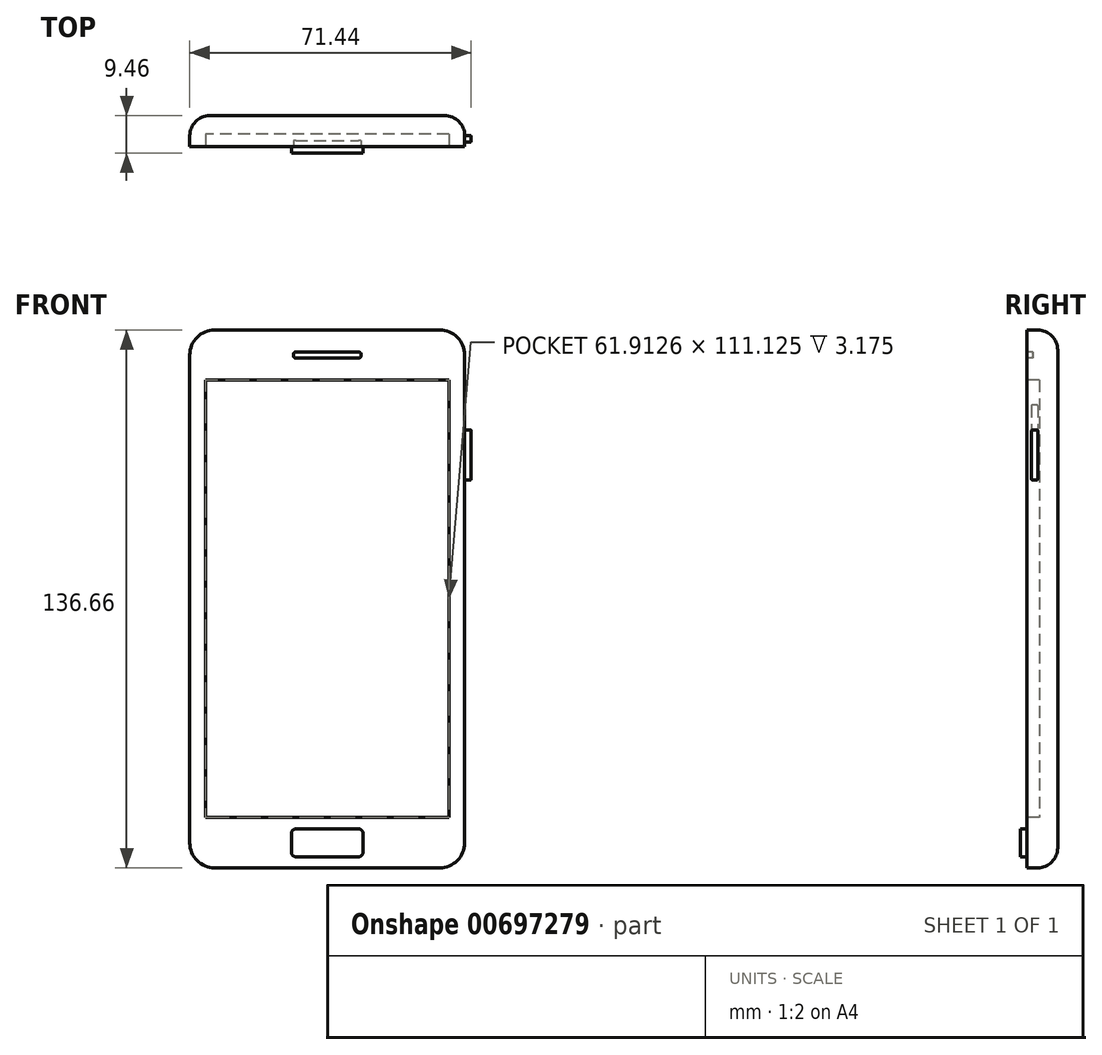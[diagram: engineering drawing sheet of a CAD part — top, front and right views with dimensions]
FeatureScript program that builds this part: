
annotation { "Feature Type Name" : "Feature", "Feature Type Description" : "" }
export const myFeature = defineFeature(function(context is Context, id is Id, definition is map)
    precondition{}
    {
        {
            var Q0;
            Q0=qCreatedBy(makeId("Front.planeOp"),FACE);
            var sketch = newSketch(context, id + "F0", { "sketchPlane" : qUnion([Q0])});
            skLineSegment(sketch, "E0", {"start": v(-34.93, 61.98) * mm, "end": v(-34.93, -61.98) * mm});
            skLineSegment(sketch, "E1", {"start": v(-28.58, 68.33) * mm, "end": v(28.57, 68.33) * mm});
            skLineSegment(sketch, "E2", {"start": v(34.92, 61.98) * mm, "end": v(34.92, -61.98) * mm});
            skLineSegment(sketch, "E3", {"start": v(28.57, -68.33) * mm, "end": v(-28.58, -68.33) * mm});
            skPoint(sketch, "E4.visualSharp", {"position": v(-34.93, 68.33) * mm});
            skArc(sketch, "E4.filletArc", {"start": v(-28.58, 68.33) * mm, "mid": v(-33.07, 66.47) * mm, "end": v(-34.93, 61.98) * mm});
            skPoint(sketch, "E5.visualSharp", {"position": v(34.92, 68.33) * mm});
            skArc(sketch, "E5.filletArc", {"start": v(34.92, 61.98) * mm, "mid": v(33.07, 66.47) * mm, "end": v(28.57, 68.33) * mm});
            skLineSegment(sketch, "E6", {"start": v(0, 68.33) * mm, "end": v(0, -68.33) * mm, "construction": true});
            skPoint(sketch, "E7.visualSharp", {"position": v(-34.93, -68.33) * mm});
            skArc(sketch, "E7.filletArc", {"start": v(-34.93, -61.98) * mm, "mid": v(-33.07, -66.47) * mm, "end": v(-28.58, -68.33) * mm});
            skPoint(sketch, "E8.visualSharp", {"position": v(34.92, -68.33) * mm});
            skArc(sketch, "E8.filletArc", {"start": v(28.57, -68.33) * mm, "mid": v(33.07, -66.47) * mm, "end": v(34.92, -61.98) * mm});
            skLineSegment(sketch, "E9", {"start": v(-34.93, 0) * mm, "end": v(34.92, 0) * mm, "construction": true});
            skLineSegment(sketch, "E10", {"start": v(-34.93, -61.98) * mm, "end": v(34.92, -61.98) * mm, "construction": true});
            skLineSegment(sketch, "E11", {"start": v(-34.93, 61.98) * mm, "end": v(34.92, 61.98) * mm, "construction": true});
            skSolve(sketch);
        }
        {
            var Q0;
            Q0=makeQuery(id+"F0.imprint","IMPRINT",FACE,{"disambiguationData":[TD([[makeQuery(id+"F0.imprint","IMPRINT",EDGE,{"derivedFrom":sQuery(id+"F0.wireOp",EDGE,"E0")}),1.0]])]});
            var Q1;
            Q1=makeQuery(id+"F0.imprint","IMPRINT",FACE,{"disambiguationData":[TD([[makeQuery(id+"F0.imprint","IMPRINT",EDGE,{"derivedFrom":sQuery(id+"F0.wireOp",EDGE,"Yxqkso8f-ke1d-uWKi-IK2T-4UMQfv2AGNoA")}),-1.0]])]});
            var Q2;
            Q2=makeQuery(id+"F0.imprint","IMPRINT",FACE,{"disambiguationData":[TD([[makeQuery(id+"F0.imprint","IMPRINT",EDGE,{"derivedFrom":sQuery(id+"F0.wireOp",EDGE,"Q10cRNlM-3Szw-gUv3-p6k7-crAdpTybPVzU")}),-1.0]])]});
            extrude(context, id + "F1", {"entities" : qUnion([Q0, Q1, Q2]), "depth" : 7.87 * mm, "offsetDistance" : 25.4 * mm});
        }
        {
            var Q0;
            Q0=makeQuery(id+"F1.opExtrude","CAP_EDGE",EDGE,{"disambiguationData":[OSD([sQuery(id+"F0.wireOp",EDGE,"E5.filletArc")])],"isStart":true});
            var Q1;
            Q1=makeQuery(id+"F1.opExtrude","CAP_EDGE",EDGE,{"disambiguationData":[OSD([sQuery(id+"F0.wireOp",EDGE,"E1")])],"isStart":true});
            var Q2;
            Q2=makeQuery(id+"F1.opExtrude","CAP_EDGE",EDGE,{"disambiguationData":[OSD([sQuery(id+"F0.wireOp",EDGE,"E2")])],"isStart":true});
            fillet(context, id + "F2", {"entities" : qUnion([Q0, Q1, Q2]), "radius" : 5.08 * mm, "tangentPropagation" : true, "allowEdgeOverflow" : false});
        }
        {
            var Q0;
            Q0=makeQuery(id+"F1.opExtrude","CAP_FACE",FACE,{"disambiguationData":[OSD([sQuery(id+"F0.wireOp",EDGE,"E0"),sQuery(id+"F0.wireOp",EDGE,"E1"),sQuery(id+"F0.wireOp",EDGE,"E2"),sQuery(id+"F0.wireOp",EDGE,"E3"),sQuery(id+"F0.wireOp",EDGE,"E4.filletArc"),sQuery(id+"F0.wireOp",EDGE,"E5.filletArc"),sQuery(id+"F0.wireOp",EDGE,"E7.filletArc"),sQuery(id+"F0.wireOp",EDGE,"E8.filletArc"),sQuery(id+"F0.wireOp",EDGE,"Yxqkso8f-ke1d-uWKi-IK2T-4UMQfv2AGNoA"),sQuery(id+"F0.wireOp",EDGE,"wvmofA8N-cZgQ-HB6A-NeT5-mTsQP75NdnSN"),sQuery(id+"F0.wireOp",EDGE,"2k0ZVNAU-dHE0-9XoG-fVzd-rWTm6Z1FSZgh"),sQuery(id+"F0.wireOp",EDGE,"L0vu10QN-11z5-3LHw-4cct-LfvSpySfau56"),sQuery(id+"F0.wireOp",EDGE,"61cbf7f2-a8a0-450c-8582-404ff57eee1e.filletArc"),sQuery(id+"F0.wireOp",EDGE,"9b09c1d2-0208-4afe-876b-a53897a61bd5.filletArc"),sQuery(id+"F0.wireOp",EDGE,"2e49db2c-9e25-4e03-abbd-2e55815f41f9.filletArc"),sQuery(id+"F0.wireOp",EDGE,"847fe96b-3720-45e1-b239-618744106075.filletArc"),sQuery(id+"F0.wireOp",EDGE,"Q10cRNlM-3Szw-gUv3-p6k7-crAdpTybPVzU"),sQuery(id+"F0.wireOp",EDGE,"rr5Ry5rM-HqL5-93G9-RZ6w-pYJKNWClKjOs"),sQuery(id+"F0.wireOp",EDGE,"Tm6RvqHi-hzwC-IS7W-cwuA-Y99RD3NHICGs"),sQuery(id+"F0.wireOp",EDGE,"gLD1SR3Y-jlRX-iXej-22FT-tG82X233p80r"),sQuery(id+"F0.wireOp",EDGE,"53dd5e3a-b83d-4c4f-a617-f595e198c785.filletArc"),sQuery(id+"F0.wireOp",EDGE,"2cd74231-fede-4f60-8454-4e1e7671c0d9.filletArc"),sQuery(id+"F0.wireOp",EDGE,"ae25c646-67f5-4699-874b-49e99440fea7.filletArc"),sQuery(id+"F0.wireOp",EDGE,"5c01ee20-0546-43ea-a8ab-d59d5ab6d27c.filletArc")])],"isStart":false});
            var sketch = newSketch(context, id + "F3", { "sketchPlane" : qUnion([Q0])});
            skLineSegment(sketch, "E12", {"start": v(-30.96, 55.56) * mm, "end": v(-30.96, -55.56) * mm});
            skLineSegment(sketch, "E13", {"start": v(-30.96, -55.56) * mm, "end": v(30.96, -55.56) * mm});
            skLineSegment(sketch, "E14", {"start": v(30.96, -55.56) * mm, "end": v(30.96, 55.56) * mm});
            skLineSegment(sketch, "E15", {"start": v(30.96, 55.56) * mm, "end": v(-30.96, 55.56) * mm});
            skLineSegment(sketch, "E16", {"start": v(0, 55.56) * mm, "end": v(0, -55.56) * mm, "construction": true});
            skLineSegment(sketch, "E17", {"start": v(30.96, 0) * mm, "end": v(-30.96, 0) * mm, "construction": true});
            skPoint(sketch, "E17.endSnap0", {"position": v(-34.93, 0) * mm});
            skLineSegment(sketch, "E18", {"start": v(-7.94, 62.77) * mm, "end": v(7.94, 62.77) * mm});
            skLineSegment(sketch, "E19", {"start": v(8.61, 62.1) * mm, "end": v(8.61, 61.86) * mm});
            skLineSegment(sketch, "E20", {"start": v(7.94, 61.18) * mm, "end": v(-7.94, 61.18) * mm});
            skLineSegment(sketch, "E21", {"start": v(-8.61, 61.86) * mm, "end": v(-8.61, 62.1) * mm});
            skArc(sketch, "E22.filletArc", {"start": v(8.61, 62.1) * mm, "mid": v(8.41, 62.57) * mm, "end": v(7.94, 62.77) * mm});
            skArc(sketch, "E23.filletArc", {"start": v(7.94, 61.18) * mm, "mid": v(8.41, 61.38) * mm, "end": v(8.61, 61.86) * mm});
            skArc(sketch, "E24.filletArc", {"start": v(-7.94, 62.77) * mm, "mid": v(-8.41, 62.57) * mm, "end": v(-8.61, 62.1) * mm});
            skArc(sketch, "E25.filletArc", {"start": v(-8.61, 61.86) * mm, "mid": v(-8.41, 61.38) * mm, "end": v(-7.94, 61.18) * mm});
            skLineSegment(sketch, "E26", {"start": v(0, 62.77) * mm, "end": v(0, 61.18) * mm, "construction": true});
            skLineSegment(sketch, "E27", {"start": v(8.61, 61.98) * mm, "end": v(-8.61, 61.98) * mm, "construction": true});
            skSolve(sketch);
        }
        {
            var Q0;
            Q0=makeQuery(id+"F3.imprint","IMPRINT",FACE,{"disambiguationData":[TD([[makeQuery(id+"F3.imprint","IMPRINT",EDGE,{"derivedFrom":sQuery(id+"F3.wireOp",EDGE,"E12")}),1.0]])]});
            extrude(context, id + "F4", {"entities" : qUnion([Q0]), "operationType" : NewBodyOperationType.REMOVE, "oppositeDirection" : true, "depth" : 3.17 * mm, "offsetDistance" : 25.4 * mm});
        }
        {
            var Q0;
            Q0=makeQuery(id+"F3.imprint","IMPRINT",FACE,{"disambiguationData":[TD([[makeQuery(id+"F3.imprint","IMPRINT",EDGE,{"derivedFrom":sQuery(id+"F3.wireOp",EDGE,"E12")}),-1.0]])]});
            var sketch = newSketch(context, id + "F5", { "sketchPlane" : qUnion([Q0])});
            skLineSegment(sketch, "E28", {"start": v(-7.94, -58.43) * mm, "end": v(7.94, -58.43) * mm});
            skLineSegment(sketch, "E29", {"start": v(-9.1, -59.6) * mm, "end": v(-9.1, -64.36) * mm});
            skLineSegment(sketch, "E30", {"start": v(9.1, -59.6) * mm, "end": v(9.1, -64.36) * mm});
            skLineSegment(sketch, "E31", {"start": v(7.94, -65.52) * mm, "end": v(-7.94, -65.52) * mm});
            skArc(sketch, "E32.filletArc", {"start": v(-7.94, -58.43) * mm, "mid": v(-8.76, -58.77) * mm, "end": v(-9.1, -59.6) * mm});
            skArc(sketch, "E33.filletArc", {"start": v(-9.1, -64.36) * mm, "mid": v(-8.76, -65.18) * mm, "end": v(-7.94, -65.52) * mm});
            skArc(sketch, "E34.filletArc", {"start": v(9.1, -59.6) * mm, "mid": v(8.76, -58.77) * mm, "end": v(7.94, -58.43) * mm});
            skArc(sketch, "E35.filletArc", {"start": v(7.94, -65.52) * mm, "mid": v(8.76, -65.18) * mm, "end": v(9.1, -64.36) * mm});
            skLineSegment(sketch, "E36", {"start": v(0, -58.43) * mm, "end": v(0, -65.52) * mm, "construction": true});
            skLineSegment(sketch, "E37", {"start": v(-9.1, -61.98) * mm, "end": v(9.1, -61.98) * mm, "construction": true});
            skSolve(sketch);
        }
        {
            var Q0;
            Q0=makeQuery(id+"F5.imprint","IMPRINT",FACE,{"disambiguationData":[TD([[makeQuery(id+"F5.imprint","IMPRINT",EDGE,{"derivedFrom":sQuery(id+"F5.wireOp",EDGE,"E28")}),-1.0]])]});
            extrude(context, id + "F6", {"entities" : qUnion([Q0]), "operationType" : NewBodyOperationType.ADD, "depth" : 1.59 * mm, "offsetDistance" : 25.4 * mm});
        }
        {
            var Q0;
            Q0=makeQuery(id+"F3.imprint","IMPRINT",FACE,{"disambiguationData":[TD([[makeQuery(id+"F3.imprint","IMPRINT",EDGE,{"derivedFrom":sQuery(id+"F3.wireOp",EDGE,"E18")}),-1.0]])]});
            extrude(context, id + "F7", {"entities" : qUnion([Q0]), "operationType" : NewBodyOperationType.REMOVE, "oppositeDirection" : true, "depth" : 1.59 * mm, "offsetDistance" : 25.4 * mm});
        }
        {
            var Q0;
            Q0=makeQuery(id+"F1.opExtrude","SWEPT_FACE",FACE,{"disambiguationData":[OSD([sQuery(id+"F0.wireOp",EDGE,"E0")])]});
            var sketch = newSketch(context, id + "F8", { "sketchPlane" : qUnion([Q0])});
            skLineSegment(sketch, "E38", {"start": v(6.67, 49.05) * mm, "end": v(6.67, 30.45) * mm});
            skLineSegment(sketch, "E39", {"start": v(6.44, 30.23) * mm, "end": v(5.3, 30.23) * mm});
            skLineSegment(sketch, "E40", {"start": v(5.08, 30.45) * mm, "end": v(5.08, 49.05) * mm});
            skLineSegment(sketch, "E41", {"start": v(5.3, 49.28) * mm, "end": v(6.44, 49.28) * mm});
            skLineSegment(sketch, "E42", {"start": v(6.67, 39.75) * mm, "end": v(5.08, 39.75) * mm, "construction": true});
            skPoint(sketch, "E43.visualSharp", {"position": v(6.67, 49.28) * mm});
            skArc(sketch, "E43.filletArc", {"start": v(6.67, 49.05) * mm, "mid": v(6.6, 49.2) * mm, "end": v(6.44, 49.28) * mm});
            skPoint(sketch, "E44.visualSharp", {"position": v(5.08, 49.28) * mm});
            skArc(sketch, "E44.filletArc", {"start": v(5.3, 49.28) * mm, "mid": v(5.15, 49.2) * mm, "end": v(5.08, 49.05) * mm});
            skPoint(sketch, "E45.visualSharp", {"position": v(6.67, 30.23) * mm});
            skArc(sketch, "E45.filletArc", {"start": v(6.44, 30.23) * mm, "mid": v(6.6, 30.3) * mm, "end": v(6.67, 30.45) * mm});
            skPoint(sketch, "E46.visualSharp", {"position": v(5.08, 30.23) * mm});
            skArc(sketch, "E46.filletArc", {"start": v(5.08, 30.45) * mm, "mid": v(5.15, 30.3) * mm, "end": v(5.3, 30.23) * mm});
            skSolve(sketch);
        }
        {
            var Q0;
            Q0=makeQuery(id+"F8.imprint","IMPRINT",FACE,{"disambiguationData":[TD([[makeQuery(id+"F8.imprint","IMPRINT",EDGE,{"derivedFrom":sQuery(id+"F8.wireOp",EDGE,"E41")}),-1.0]])]});
            var Q1;
            Q1=makeQuery(id+"F8.imprint","IMPRINT",FACE,{"disambiguationData":[TD([[makeQuery(id+"F8.imprint","IMPRINT",EDGE,{"derivedFrom":sQuery(id+"F8.wireOp",EDGE,"E39")}),-1.0]])]});
            extrude(context, id + "F9", {"entities" : qUnion([Q0, Q1]), "operationType" : NewBodyOperationType.ADD, "depth" : 1 / 406.4 * mm, "offsetDistance" : 25.4 * mm});
        }
        {
            var Q0;
            Q0=makeQuery(id+"F1.opExtrude","SWEPT_FACE",FACE,{"disambiguationData":[OSD([sQuery(id+"F0.wireOp",EDGE,"E2")])]});
            var sketch = newSketch(context, id + "F10", { "sketchPlane" : qUnion([Q0])});
            skLineSegment(sketch, "E47", {"start": v(-5.08, 42.7) * mm, "end": v(-5.08, 30.45) * mm});
            skLineSegment(sketch, "E48", {"start": v(-5.3, 30.23) * mm, "end": v(-6.44, 30.23) * mm});
            skLineSegment(sketch, "E49", {"start": v(-6.67, 30.45) * mm, "end": v(-6.67, 42.7) * mm});
            skLineSegment(sketch, "E50", {"start": v(-6.44, 42.93) * mm, "end": v(-5.3, 42.93) * mm});
            skLineSegment(sketch, "E51", {"start": v(-5.08, 36.58) * mm, "end": v(-6.67, 36.58) * mm, "construction": true});
            skPoint(sketch, "E52.visualSharp", {"position": v(-5.08, 42.93) * mm});
            skArc(sketch, "E52.filletArc", {"start": v(-5.08, 42.7) * mm, "mid": v(-5.15, 42.86) * mm, "end": v(-5.3, 42.93) * mm});
            skPoint(sketch, "E53.visualSharp", {"position": v(-6.67, 42.93) * mm});
            skArc(sketch, "E53.filletArc", {"start": v(-6.44, 42.93) * mm, "mid": v(-6.6, 42.86) * mm, "end": v(-6.67, 42.7) * mm});
            skPoint(sketch, "E54.visualSharp", {"position": v(-5.08, 30.23) * mm});
            skArc(sketch, "E54.filletArc", {"start": v(-5.3, 30.23) * mm, "mid": v(-5.15, 30.3) * mm, "end": v(-5.08, 30.45) * mm});
            skPoint(sketch, "E55.visualSharp", {"position": v(-6.67, 30.23) * mm});
            skArc(sketch, "E55.filletArc", {"start": v(-6.67, 30.45) * mm, "mid": v(-6.6, 30.3) * mm, "end": v(-6.44, 30.23) * mm});
            skSolve(sketch);
        }
        {
            var Q0;
            Q0=makeQuery(id+"F10.imprint","IMPRINT",FACE,{"disambiguationData":[TD([[makeQuery(id+"F10.imprint","IMPRINT",EDGE,{"derivedFrom":sQuery(id+"F10.wireOp",EDGE,"E47")}),1.0]])]});
            extrude(context, id + "F11", {"entities" : qUnion([Q0]), "operationType" : NewBodyOperationType.ADD, "depth" : 1.59 * mm, "offsetDistance" : 25.4 * mm});
        }
    });
